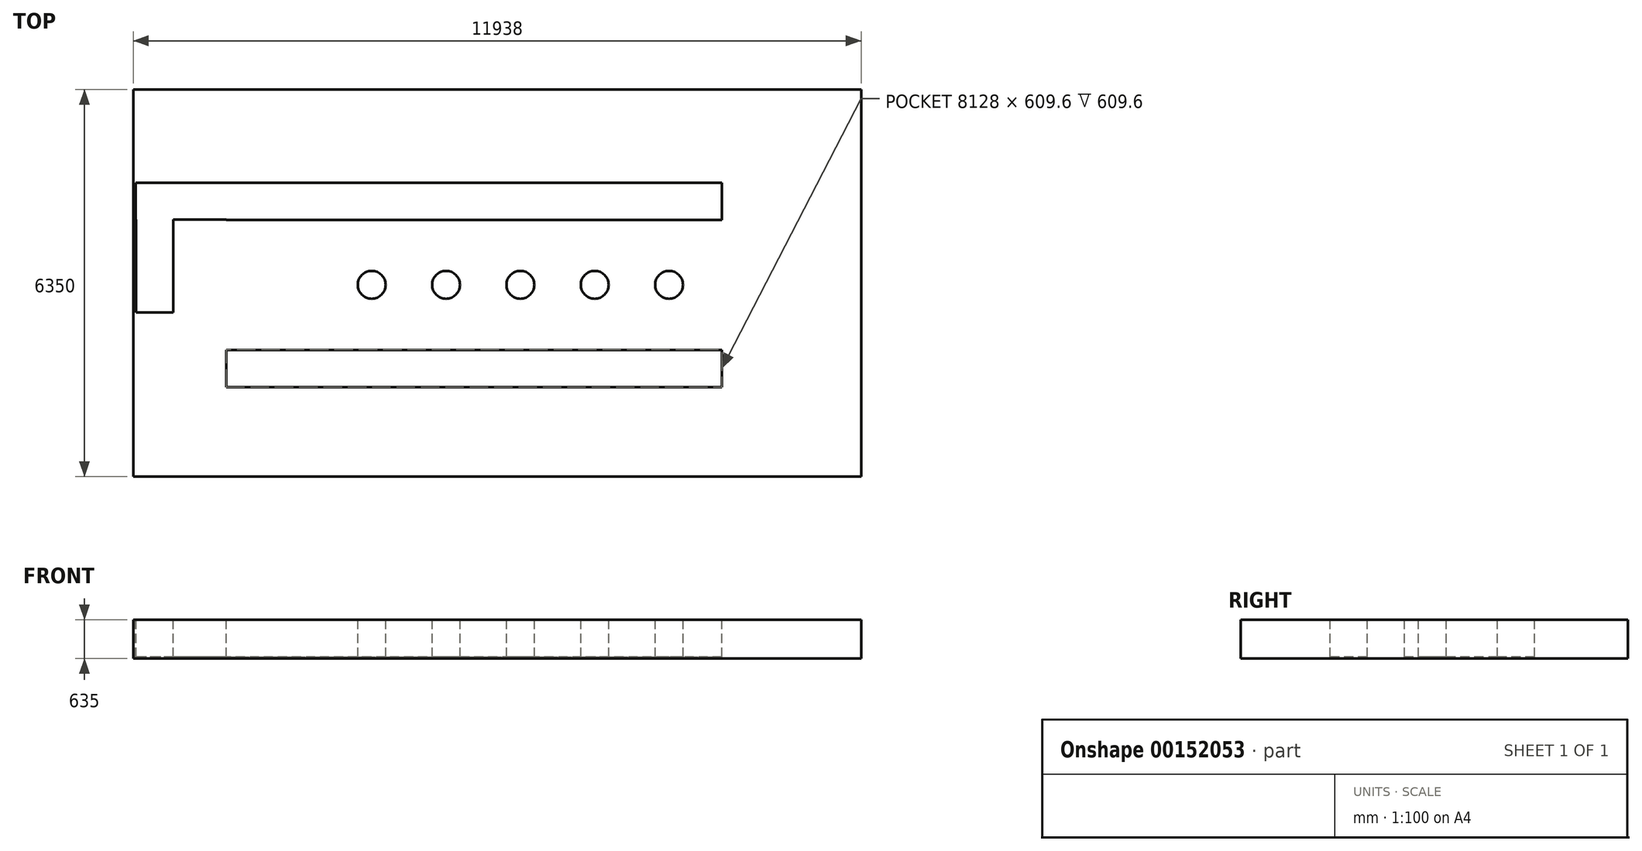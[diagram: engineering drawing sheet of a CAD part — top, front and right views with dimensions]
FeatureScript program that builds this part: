
annotation { "Feature Type Name" : "Feature", "Feature Type Description" : "" }
export const myFeature = defineFeature(function(context is Context, id is Id, definition is map)
    precondition{}
    {
        {
            var Q0;
            Q0=qCreatedBy(makeId("Top.planeOp"),FACE);
            var sketch = newSketch(context, id + "F0", { "sketchPlane" : qUnion([Q0])});
            skLineSegment(sketch, "E0", {"start": v(-1090.3, 0) * mm, "end": v(739.4, 0) * mm, "construction": true});
            skLineSegment(sketch, "E1", {"start": v(0, -260.05) * mm, "end": v(0, 282.4) * mm, "construction": true});
            skLineSegment(sketch, "E2", {"start": v(0, 282.4) * mm, "end": v(-1219.2, 282.4) * mm, "construction": true});
            skLineSegment(sketch, "E3", {"start": v(-1219.2, 0) * mm, "end": v(-1219.2, 1066.8) * mm, "construction": true});
            skLineSegment(sketch, "E4", {"start": v(-1219.2, 1066.8) * mm, "end": v(0, 1066.8) * mm, "construction": true});
            skLineSegment(sketch, "E5", {"start": v(0, 1066.8) * mm, "end": v(0, -1066.8) * mm, "construction": true});
            skLineSegment(sketch, "E6", {"start": v(0, -1066.8) * mm, "end": v(1219.2, -1066.8) * mm, "construction": true});
            skLineSegment(sketch, "E7", {"start": v(1219.2, -1066.8) * mm, "end": v(1219.2, 1066.8) * mm, "construction": true});
            skLineSegment(sketch, "E8", {"start": v(1219.2, 1066.8) * mm, "end": v(2438.4, 1066.8) * mm, "construction": true});
            skLineSegment(sketch, "E9", {"start": v(2438.4, 1066.8) * mm, "end": v(2438.4, -1066.8) * mm, "construction": true});
            skLineSegment(sketch, "E10", {"start": v(2438.4, -1066.8) * mm, "end": v(3657.6, -1066.8) * mm, "construction": true});
            skLineSegment(sketch, "E11", {"start": v(3657.6, -1066.8) * mm, "end": v(3657.6, 1066.8) * mm, "construction": true});
            skLineSegment(sketch, "E12", {"start": v(-1219.2, 0) * mm, "end": v(-1219.2, -1066.8) * mm, "construction": true});
            skLineSegment(sketch, "E13", {"start": v(739.4, 0) * mm, "end": v(4080.02, 0) * mm, "construction": true});
            skLineSegment(sketch, "E14.bottom", {"start": v(-3606.8, -1066.8) * mm, "end": v(4521.2, -1066.8) * mm});
            skLineSegment(sketch, "E14.top", {"start": v(-3606.8, -1676.4) * mm, "end": v(4521.2, -1676.4) * mm});
            skLineSegment(sketch, "E14.left", {"start": v(-3606.8, -1066.8) * mm, "end": v(-3606.8, -1676.4) * mm});
            skLineSegment(sketch, "E14.right", {"start": v(4521.2, -1066.8) * mm, "end": v(4521.2, -1676.4) * mm});
            skLineSegment(sketch, "E15.bottom", {"start": v(-3606.8, 1066.8) * mm, "end": v(4521.2, 1066.8) * mm});
            skLineSegment(sketch, "E15.top", {"start": v(-3606.8, 1676.4) * mm, "end": v(4521.2, 1676.4) * mm});
            skLineSegment(sketch, "E15.left", {"start": v(-3606.8, 1066.8) * mm, "end": v(-3606.8, 1676.4) * mm});
            skLineSegment(sketch, "E15.right", {"start": v(4521.2, 1066.8) * mm, "end": v(4521.2, 1676.4) * mm});
            skLineSegment(sketch, "E16.bottom", {"start": v(-5130.8, 3204.6) * mm, "end": v(6807.2, 3204.6) * mm});
            skLineSegment(sketch, "E16.top", {"start": v(-5130.8, -3145.4) * mm, "end": v(6807.2, -3145.4) * mm});
            skLineSegment(sketch, "E16.left", {"start": v(-5130.8, 3204.6) * mm, "end": v(-5130.8, -3145.4) * mm});
            skLineSegment(sketch, "E16.right", {"start": v(6807.2, 3204.6) * mm, "end": v(6807.2, -3145.4) * mm});
            skLineSegment(sketch, "E17.bottom", {"start": v(-3606.8, 1676.4) * mm, "end": v(-5091.78, 1676.4) * mm});
            skLineSegment(sketch, "E17.top", {"start": v(-3606.8, 1067.64) * mm, "end": v(-5091.78, 1067.64) * mm});
            skLineSegment(sketch, "E17.left", {"start": v(-3606.8, 1676.4) * mm, "end": v(-3606.8, 1067.64) * mm});
            skLineSegment(sketch, "E17.right", {"start": v(-5091.78, 1676.4) * mm, "end": v(-5091.78, 1067.64) * mm});
            skLineSegment(sketch, "E18.bottom", {"start": v(-5091.78, 1067.64) * mm, "end": v(-4473.71, 1067.64) * mm});
            skLineSegment(sketch, "E18.top", {"start": v(-5091.78, 1067.64) * mm, "end": v(-4473.71, 1067.64) * mm});
            skLineSegment(sketch, "E18.left", {"start": v(-5091.78, 1067.64) * mm, "end": v(-5091.78, 1067.64) * mm});
            skLineSegment(sketch, "E18.right", {"start": v(-4473.71, 1067.64) * mm, "end": v(-4473.71, 1067.64) * mm});
            skLineSegment(sketch, "E19.bottom", {"start": v(-4473.71, 1067.64) * mm, "end": v(-5083.31, 1067.64) * mm});
            skLineSegment(sketch, "E19.top", {"start": v(-4473.71, -456.36) * mm, "end": v(-5083.31, -456.36) * mm});
            skLineSegment(sketch, "E19.left", {"start": v(-4473.71, 1067.64) * mm, "end": v(-4473.71, -456.36) * mm});
            skLineSegment(sketch, "E19.right", {"start": v(-5083.31, 1067.64) * mm, "end": v(-5083.31, -456.36) * mm});
            skSolve(sketch);
        }
        {
            var Q0;
            Q0 = qSketchRegion(id + "F0", true);
            extrude(context, id + "F1", {"entities" : qUnion([Q0]), "oppositeDirection" : true, "depth" : 609.6 * mm});
        }
        {
            var Q0;
            Q0=makeQuery(id+"F0.imprint","IMPRINT",FACE,{"disambiguationData":[TD([[makeQuery(id+"F0.imprint","IMPRINT",EDGE,{"derivedFrom":sQuery(id+"F0.wireOp",EDGE,"E14.bottom")}),1.0]])]});
            var sketch = newSketch(context, id + "F2", { "sketchPlane" : qUnion([Q0])});
            skCircle(sketch, "E20", {"center": v(0, 0) * mm, "radius": 228.6 * mm});
            skCircle(sketch, "E21", {"center": v(-1219.2, 0) * mm, "radius": 228.6 * mm});
            skCircle(sketch, "E22", {"center": v(1219.2, 0) * mm, "radius": 228.6 * mm});
            skCircle(sketch, "E23", {"center": v(2438.4, 0) * mm, "radius": 228.6 * mm});
            skCircle(sketch, "E24", {"center": v(3657.6, 0) * mm, "radius": 228.6 * mm});
            skSolve(sketch);
        }
        {
            var Q0;
            Q0 = qSketchRegion(id + "F2", true);
            extrude(context, id + "F3", {"entities" : qUnion([Q0]), "operationType" : NewBodyOperationType.REMOVE, "endBound" : BoundingType.THROUGH_ALL, "oppositeDirection" : true, "depth" : 25.4 * mm});
        }
        {
            var Q0;
            Q0=makeQuery(id+"F1.opExtrude","CAP_FACE",FACE,{"disambiguationData":[OSD([sQuery(id+"F0.wireOp",EDGE,"E14.bottom"),sQuery(id+"F0.wireOp",EDGE,"E14.top"),sQuery(id+"F0.wireOp",EDGE,"E14.left"),sQuery(id+"F0.wireOp",EDGE,"E14.right"),sQuery(id+"F0.wireOp",EDGE,"E15.bottom"),sQuery(id+"F0.wireOp",EDGE,"E15.top"),sQuery(id+"F0.wireOp",EDGE,"E15.left"),sQuery(id+"F0.wireOp",EDGE,"E15.right"),sQuery(id+"F0.wireOp",EDGE,"E16.bottom"),sQuery(id+"F0.wireOp",EDGE,"E16.top"),sQuery(id+"F0.wireOp",EDGE,"E16.left"),sQuery(id+"F0.wireOp",EDGE,"E16.right"),sQuery(id+"F0.wireOp",EDGE,"E17.bottom"),sQuery(id+"F0.wireOp",EDGE,"E17.top"),sQuery(id+"F0.wireOp",EDGE,"E17.right"),sQuery(id+"F0.wireOp",EDGE,"E18.top"),sQuery(id+"F0.wireOp",EDGE,"E19.top"),sQuery(id+"F0.wireOp",EDGE,"E19.left"),sQuery(id+"F0.wireOp",EDGE,"E19.right")])],"isStart":false});
            var sketch = newSketch(context, id + "F4", { "sketchPlane" : qUnion([Q0])});
            skLineSegment(sketch, "E25.bottom", {"start": v(-5130.8, 3145.4) * mm, "end": v(6807.2, 3145.4) * mm});
            skLineSegment(sketch, "E25.top", {"start": v(-5130.8, -3204.6) * mm, "end": v(6807.2, -3204.6) * mm});
            skLineSegment(sketch, "E25.left", {"start": v(-5130.8, 3145.4) * mm, "end": v(-5130.8, -3204.6) * mm});
            skLineSegment(sketch, "E25.right", {"start": v(6807.2, 3145.4) * mm, "end": v(6807.2, -3204.6) * mm});
            skSolve(sketch);
        }
        {
            var Q0;
            Q0 = qSketchRegion(id + "F4", true);
            extrude(context, id + "F5", {"entities" : qUnion([Q0]), "operationType" : NewBodyOperationType.ADD, "depth" : 25.4 * mm});
        }
    });
